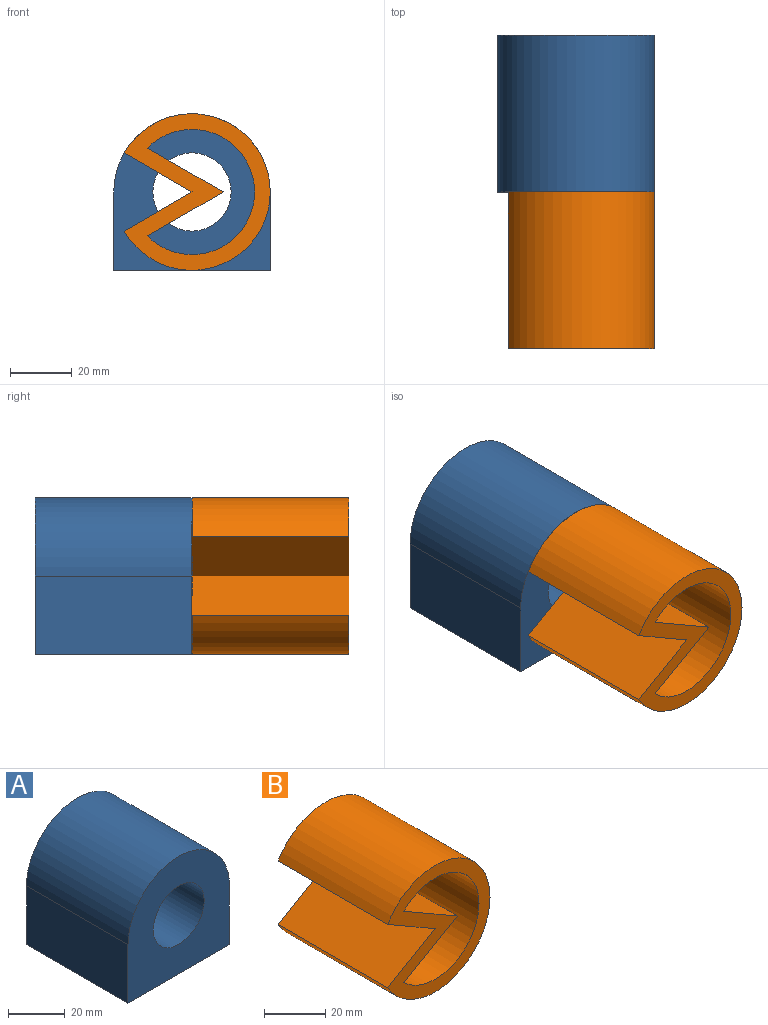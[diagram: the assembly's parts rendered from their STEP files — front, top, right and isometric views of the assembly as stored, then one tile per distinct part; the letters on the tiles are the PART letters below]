
ASSEMBLY  parts=2 mates=1
PART A: 7 faces, bbox 50.8x50.8x50.8 mm
  f0: cylinder r=25.4mm len=50.8mm, axis (0,1,0), area 4053.7mm2, adj f1,f3,f4,f5
  f1: plane 50.8x25.4mm, normal (-1,0,0), area 1290.3mm2, adj f0,f2,f4,f5
  f2: plane 50.8x50.8mm, normal (0,0,-1), area 2580.6mm2, adj f1,f3,f4,f5
  f3: plane 50.8x25.4mm, normal (1,0,0), area 1290.3mm2, adj f0,f2,f4,f5
  f4: plane 50.8x50.8mm, normal (0,-1,0), area 1797mm2, adj f0,f1,f2,f3,f6
  f5: plane 50.8x50.8mm, normal (0,1,0), area 1797mm2, adj f0,f1,f2,f3,f6
  f6: cylinder r=12.7mm len=50.8mm, axis (0,-1,0), area 4053.7mm2, adj f4,f5
PART B: 8 faces, bbox 47.4x50.8x50.8 mm
  f0: plane 50.8x47.4mm, normal (0,-1,0), area 857mm2, adj f1,f3,f4,f5,f6,f7
  f1: cylinder r=25.4mm len=50.8mm, axis (0,-1,0), area 6756.1mm2, adj f0,f2,f3,f4
  f2: plane 50.8x47.4mm, normal (0,1,0), area 857mm2, adj f1,f3,f4,f5,f6,f7
  f3: plane 50.8x22mm, normal (-0.5,0,0.87), area 1290.3mm2, adj f0,f1,f2,f4
  f4: plane 50.8x22mm, normal (-0.5,0,-0.87), area 1290.3mm2, adj f0,f1,f2,f3
  f5: cylinder r=20.32mm len=50.8mm, axis (0,-1,0), area 4883.2mm2, adj f0,f2,f6,f7
  f6: plane 50.8x24.66mm, normal (0.5,0,-0.87), area 1446.5mm2, adj f0,f2,f5,f7
  f7: plane 50.8x24.66mm, normal (0.5,0,0.87), area 1446.5mm2, adj f0,f2,f5,f6
PLACE A t=(-25.53,6.48,6.42)mm
PLACE B t=(50.67,-44.32,31.82)mm
MATE cylindrical B.f1 <-> A.f0  axis (0,-1,0) through (-25.53,-18.92,31.82)mm
